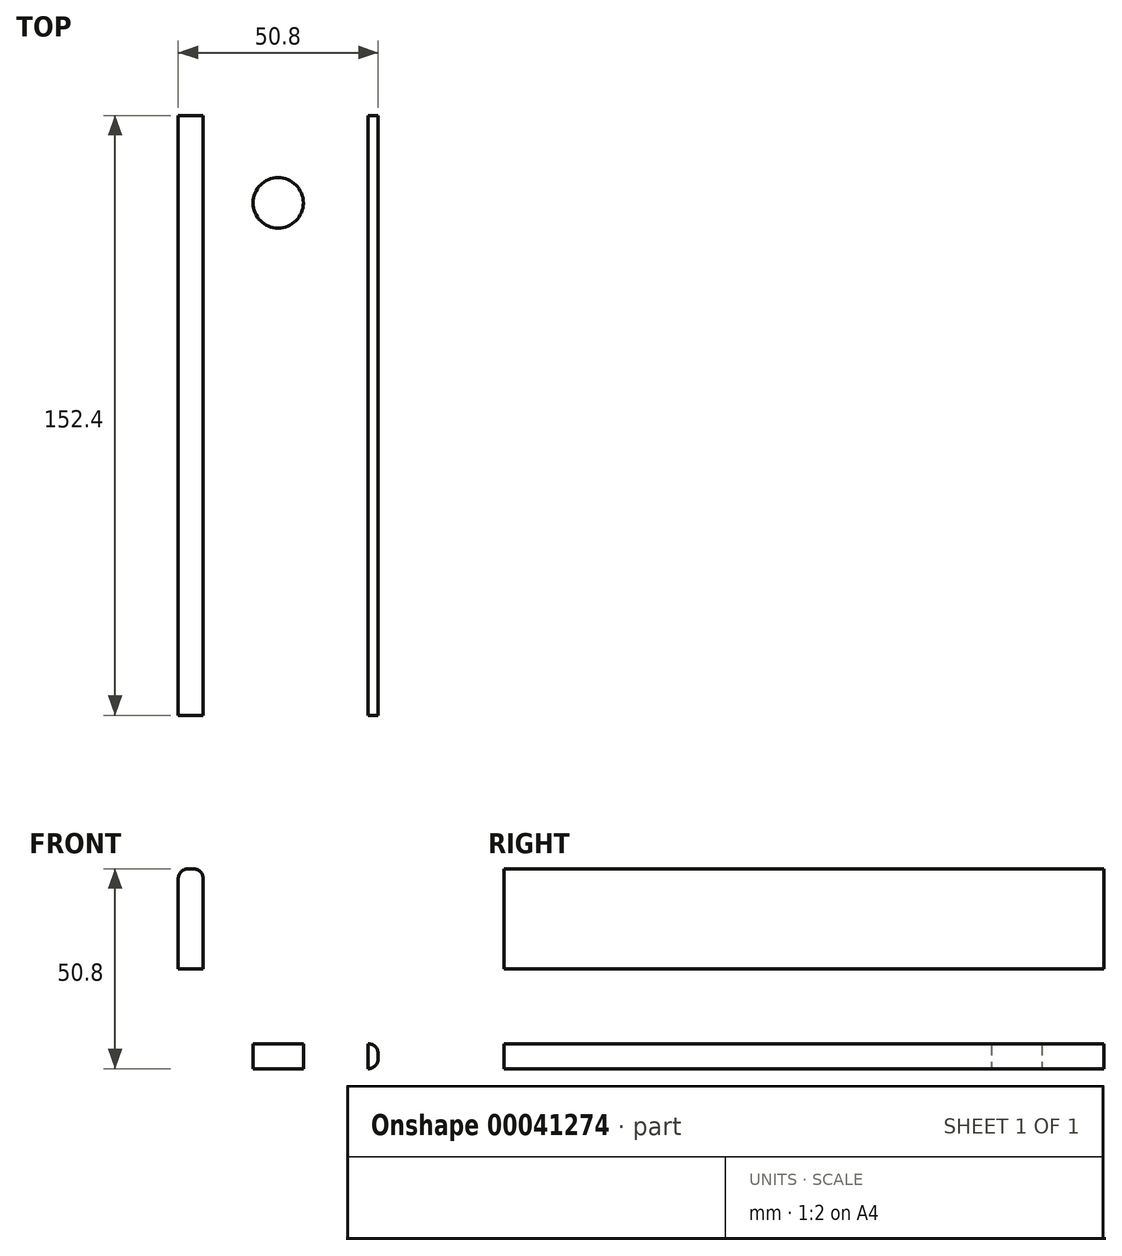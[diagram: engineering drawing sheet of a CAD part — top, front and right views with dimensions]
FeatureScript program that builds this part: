
annotation { "Feature Type Name" : "Feature", "Feature Type Description" : "" }
export const myFeature = defineFeature(function(context is Context, id is Id, definition is map)
    precondition{}
    {
        {
            var Q0;
            Q0=qCreatedBy(makeId("Front.planeOp"),FACE);
            var sketch = newSketch(context, id + "F0", { "sketchPlane" : qUnion([Q0])});
            skLineSegment(sketch, "E0", {"start": v(0, 0) * mm, "end": v(0, -50.8) * mm});
            skLineSegment(sketch, "E1", {"start": v(0, -50.8) * mm, "end": v(50.8, -50.8) * mm});
            skLineSegment(sketch, "E2", {"start": v(50.8, -50.8) * mm, "end": v(50.8, -44.45) * mm});
            skLineSegment(sketch, "E3", {"start": v(50.8, -44.45) * mm, "end": v(6.35, -44.45) * mm});
            skLineSegment(sketch, "E4", {"start": v(6.35, -44.45) * mm, "end": v(6.35, 0) * mm});
            skLineSegment(sketch, "E5", {"start": v(6.35, 0) * mm, "end": v(0, 0) * mm});
            skSolve(sketch);
        }
        {
            var Q0;
            Q0=makeQuery(id+"F0.imprint","IMPRINT",FACE,{"disambiguationData":[TD([[makeQuery(id+"F0.imprint","IMPRINT",EDGE,{"derivedFrom":sQuery(id+"F0.wireOp",EDGE,"E0")}),1.0]])]});
            extrude(context, id + "F1", {"entities" : qUnion([Q0]), "depth" : 152.4 * mm});
        }
        {
            var Q0;
            Q0=makeQuery(id+"F1.opExtrude","SWEPT_EDGE",EDGE,{"disambiguationData":[OSD([sQuery(id+"F0.wireOp",EDGE,"E4"),sQuery(id+"F0.wireOp",EDGE,"E5")])]});
            var Q1;
            Q1=makeQuery(id+"F1.opExtrude","SWEPT_EDGE",EDGE,{"disambiguationData":[OSD([sQuery(id+"F0.wireOp",EDGE,"E0"),sQuery(id+"F0.wireOp",EDGE,"E5")])]});
            var Q2;
            Q2=makeQuery(id+"F1.opExtrude","SWEPT_EDGE",EDGE,{"disambiguationData":[OSD([sQuery(id+"F0.wireOp",EDGE,"E2"),sQuery(id+"F0.wireOp",EDGE,"E3")])]});
            var Q3;
            Q3=makeQuery(id+"F1.opExtrude","SWEPT_EDGE",EDGE,{"disambiguationData":[OSD([sQuery(id+"F0.wireOp",EDGE,"E1"),sQuery(id+"F0.wireOp",EDGE,"E2")])]});
            fillet(context, id + "F2", {"entities" : qUnion([Q0, Q1, Q2, Q3]), "radius" : 2.54 * mm, "tangentPropagation" : true, "allowEdgeOverflow" : false});
        }
        {
            var Q0;
            Q0=makeQuery(id+"F1.opExtrude","SWEPT_EDGE",EDGE,{"disambiguationData":[OSD([sQuery(id+"F0.wireOp",EDGE,"E3"),sQuery(id+"F0.wireOp",EDGE,"E4")])]});
            fillet(context, id + "F3", {"entities" : qUnion([Q0]), "radius" : 4.78 * mm, "tangentPropagation" : true, "allowEdgeOverflow" : false});
        }
        {
            var Q0;
            Q0=makeQuery(id+"F1.opExtrude","SWEPT_FACE",FACE,{"disambiguationData":[OSD([sQuery(id+"F0.wireOp",EDGE,"E1")])]});
            var sketch = newSketch(context, id + "F4", { "sketchPlane" : qUnion([Q0])});
            skLineSegment(sketch, "E6", {"start": v(0, 76.2) * mm, "end": v(61.13, 76.2) * mm, "construction": true});
            skCircle(sketch, "E7", {"center": v(25.4, 130.18) * mm, "radius": 6.39 * mm});
            skCircle(sketch, "E8.MirrorC", {"center": v(25.4, 22.23) * mm, "radius": 6.39 * mm});
            skSolve(sketch);
        }
        {
            var Q0;
            Q0=makeQuery(id+"F4.imprint","IMPRINT",FACE,{"disambiguationData":[TD([[makeQuery(id+"F4.imprint","IMPRINT",EDGE,{"derivedFrom":sQuery(id+"F4.wireOp",EDGE,"E7")}),1.0]])]});
            var Q1;
            Q1=makeQuery(id+"F4.imprint","IMPRINT",FACE,{"disambiguationData":[TD([[makeQuery(id+"F4.imprint","IMPRINT",EDGE,{"derivedFrom":sQuery(id+"F4.wireOp",EDGE,"E8.MirrorC")}),-1.0]])]});
            extrude(context, id + "F5", {"entities" : qUnion([Q0, Q1]), "operationType" : NewBodyOperationType.REMOVE, "oppositeDirection" : true, "depth" : 25.4 * mm});
        }
    });
